# Revit family: Fountain-Acorn-LR1670-1-03
name_source: partatom
category: Plumbing Fixtures
revit_build: Autodesk Revit 2016 (Build: 20150714_1515(x64)
units: mm (PartAtom-declared; Revit-internal decimal feet)

## family parameters
Cut with Voids When Loaded = No
Host = Face
OmniClass Number = 23.65.70.14.11
OmniClass Title = Drinking Fountains/Coolers
Part Type = Normal
Room Calculation Point = No
Round Connector Dimension = Use Diameter
Shared = Yes

## types (1)
- LR1670-1-03
    -LWE Lavy Waste Extension (3" Standard), Specify Length Beyond Fixture = No
    -TF Transformer, 120VAC to 24VAC (-MVC option only) = No
    03 Single Temp, Non-Metering = Yes
    1 - Off-Floor, Wall Outlet = Yes
    Assembly Code = D2010810
    BRS - Brass Body Valve = No
    CW Connection = Yes
    CWFU = 1.5
    Connection Size = 1 1/2"
    Default Elevation = 40"
    Description = Acorn - Ligature Resistant LR1670 Series Drinking Fountain
    EG - Enviro-Glaze Color = No
    EVS1 - Electronic Valve System - Single Temp = No
    EVSP1 - Electronic Valve System w/ Piezo Pushbutton = No
    FMT - Fixture Mounted Trim = No
    HW Connection = Yes
    HWFU = 1.5
    Height = 13"
    Inlet Diameter Connection = 3/8"
    LR1670 Ligature Resistant Drinking Fountain = Yes
    LW1 - Lavy Through-Wall Extension With P-Trap = No
    Length = 12"
    MA2 - Manifolded, 2-Stack = No
    MA3 - Manifolded, 3-Stack = No
    MA4 - Manifolded, 4-Stack = No
    MT - Metal Template (only 1 reqd per project) = No
    MTP1 - Single Temp = No
    MTPP1 - Single Temp, Piezo Button = No
    MVC1 - Time-Trol - Single Temp = No
    MVC1-BAT - Time-Trol - Single Temp - Battery Operation = No
    Manufacturer = Acorn
    Material = 14 gage, type 304 Stainless steel
    Model = LR1670-1-03
    PFB - Power Failure Bypass (Provides drinking water in the event of power failure) = No
    PPZ1 - Programmable Piezo Pushbutton (Single Temperature Only) = No
    PT - P-Trap Waste = No
    Product Documentation Link = https://www.acorneng.com
    Product URL = https://www.acorneng.com
    Revised Date = 6/11/20
    SW - Wall Sleeve = No
    TG - 12 Gage Cabinet = No
    URL = http://www.acorneng.com
    VAC - AcornVac System = No
    Vent Connection = No
    WFU = 3
    Warranty Documentation Link = www.acorneng.com/terms-and-conditions
    Waste Connection = Yes
    Width = 22"

## geometry (parser evidence)
native form markers: Sweep x2
no freeform markers — native parametric forms only
